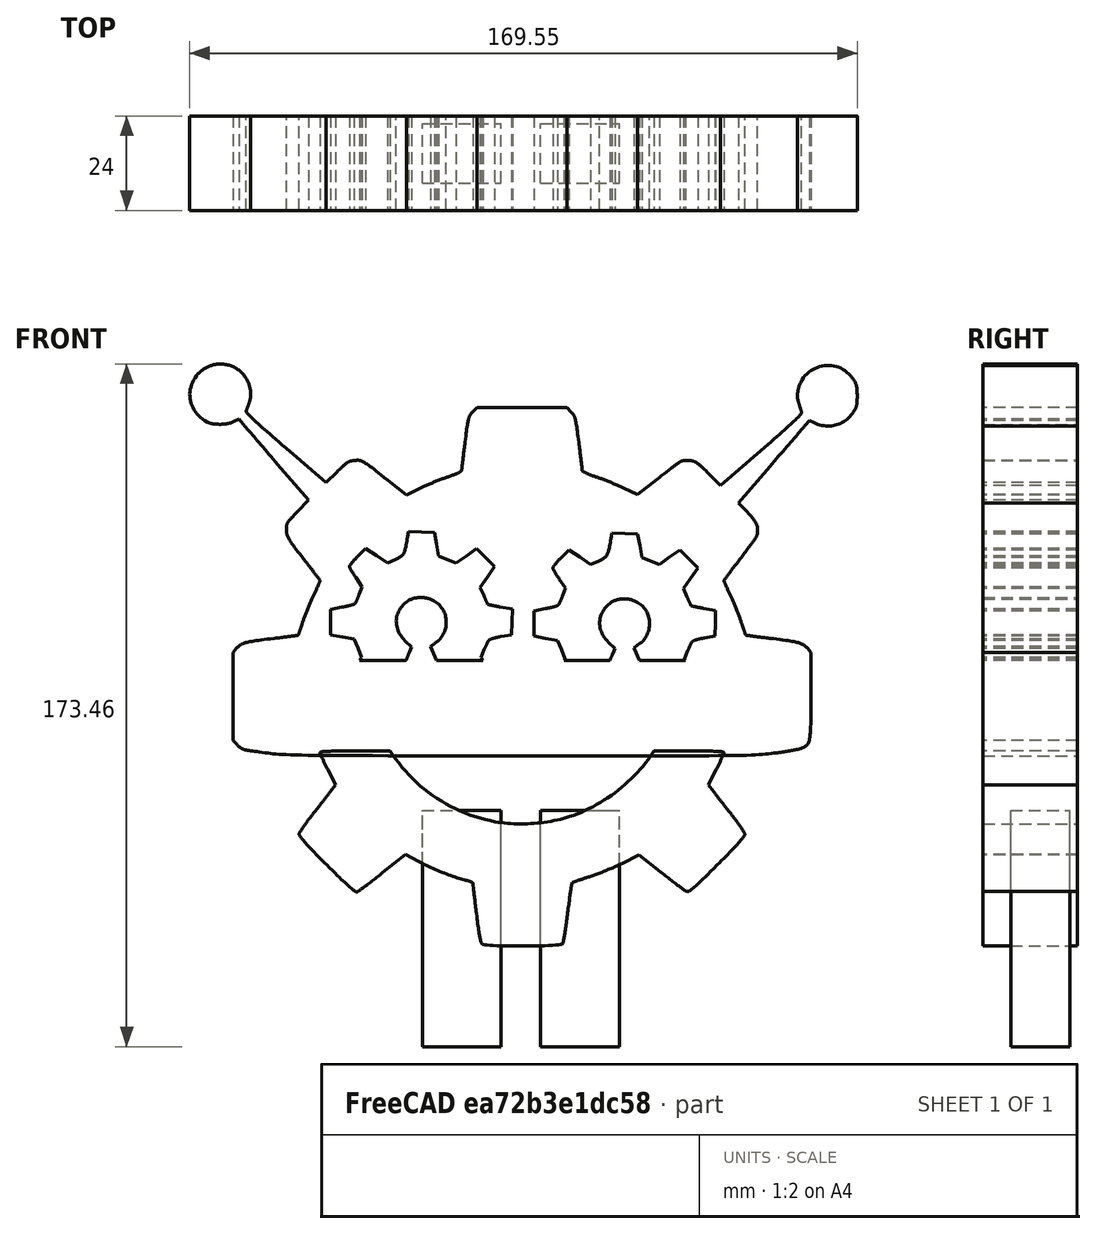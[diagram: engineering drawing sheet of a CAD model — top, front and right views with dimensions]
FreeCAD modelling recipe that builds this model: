
FCSTD DOCUMENT  (FreeCAD 0.15R4671 (Git))
Label: logo_otto
License: All rights reserved
LicenseURL: http://es.wikipedia.org/wiki/Todos_los_derechos_reservados
objects: Part::Feature×4, Part::Extrusion×4, Part::Box×2, Mesh::Feature×1
note: 10 computed .brp shape members not serialized (recipe doc carries the construction recipe); baked Part::Feature solids carry a one-line shape summary decoded from their .brp

FEATURE [Mesh::Feature] OTTO_static__1_  label="OTTO_static (1)"
FEATURE [Part::Feature] path3415
  shape: bbox 170.1 x 99.8 x 2e-07 mm, 1 faces, 0 solids (baked)
FEATURE [Part::Feature] path3415001
  shape: bbox 46.17 x 32.76 x 2e-07 mm, 1 faces, 0 solids (baked)
FEATURE [Part::Feature] path3415002
  shape: bbox 46.17 x 32.4 x 2e-07 mm, 1 faces, 0 solids (baked)
FEATURE [Part::Feature] path3415003
  shape: bbox 113.3 x 49.77 x 2e-07 mm, 1 faces, 0 solids (baked)
FEATURE [Part::Extrusion] Extrude
  Base = -> path3415
  Dir = (0,0,24)
  Placement = pos=(-80,11,94) rot=(-1,0,0;4.71239rad)
  Solid = true
FEATURE [Part::Extrusion] Extrude001
  Base = -> path3415001
  Dir = (0,0,24)
  Placement = pos=(-80,11,94) rot=(-1,0,0;4.71239rad)
  Solid = true
FEATURE [Part::Extrusion] Extrude002
  Base = -> path3415002
  Dir = (0,0,24)
  Placement = pos=(-80,11,94) rot=(-1,0,0;4.71239rad)
  Solid = true
FEATURE [Part::Extrusion] Extrude003
  Base = -> path3415003
  Dir = (0,0,24)
  Placement = pos=(-80,11,101) rot=(-1,0,0;4.71239rad)
  Solid = true
FEATURE [Part::Box] Box  label="Cubo"
  Height = 60
  Length = 20
  Placement = pos=(-20,-6,-84) rot=(0,0,1;0rad)
  Width = 15
FEATURE [Part::Box] Box001  label="Cubo001"
  Height = 60
  Length = 20
  Placement = pos=(10,-6,-84) rot=(0,0,1;0rad)
  Width = 15
